# Revit family: WALL LIGHT 03_LK2407WW
name_source: partatom
category: Luminarias
units: mm (PartAtom-declared; Revit-internal decimal feet)

## family parameters
Compartido = No
Corte con vacíos al cargar = No
Cota de conector redondo = Diámetro de uso
Origen de luz = Sí
Punto de cálculo de habitación = No
Se basa en plano de trabajo = Sí
Siempre vertical = No
Tipo de pieza = Normal

## types (1)
- WALL LIGHT 03_LK2407WW
    Archivo de red fotométrica = LK2407WW.IES
    Cambio de temperatura de color de luz atenuada = <Ninguno>
    Comentarios de vataje = 100-240V
    Descripción = LUMINARIA TIPO RECTANGULAR PARA EMPOTRAR EN MURO CON CUERPO DE ALUMINIO FUNDIDO A PRESION CUBIERTO CON POLVO GRIS OSCURO, IP 65 USO PARA INTERIORES O EXTERIORES CON CUERPO DE 1KG, CUENTA CON 24 LED TIPO SMD3020 CON UNA POTENCIA TOTAL DE 4.8W, A UNA TEMPERATURA EN BLANCO CALIDO 3000K CON 68 LUMENES, EFICIENCIA DE 14.16LM/W, IRC 80, IK10,  APERTURA A 120 GRADOS EN STOCK, 36mA EN CORRIENTE DE OPERACIÓN, ALIMENTADA A 100-240V.
    Elevación por defecto = 0 mm  [stored 0 ft]
    Fabricante = BRILLANT
    Filtro de color = 16777215
    Lámpara = SMD 3020
    Modelo = LK2407WW
    Watt per fixture = 4.8
    Ángulo de inclinación = 60.00°

note: [stored X ft] marks values corroborated as IEEE doubles in the binary element streams (Revit-internal decimal feet)

## geometry (parser evidence)
native form markers: Blend x2
no freeform markers — native parametric forms only
